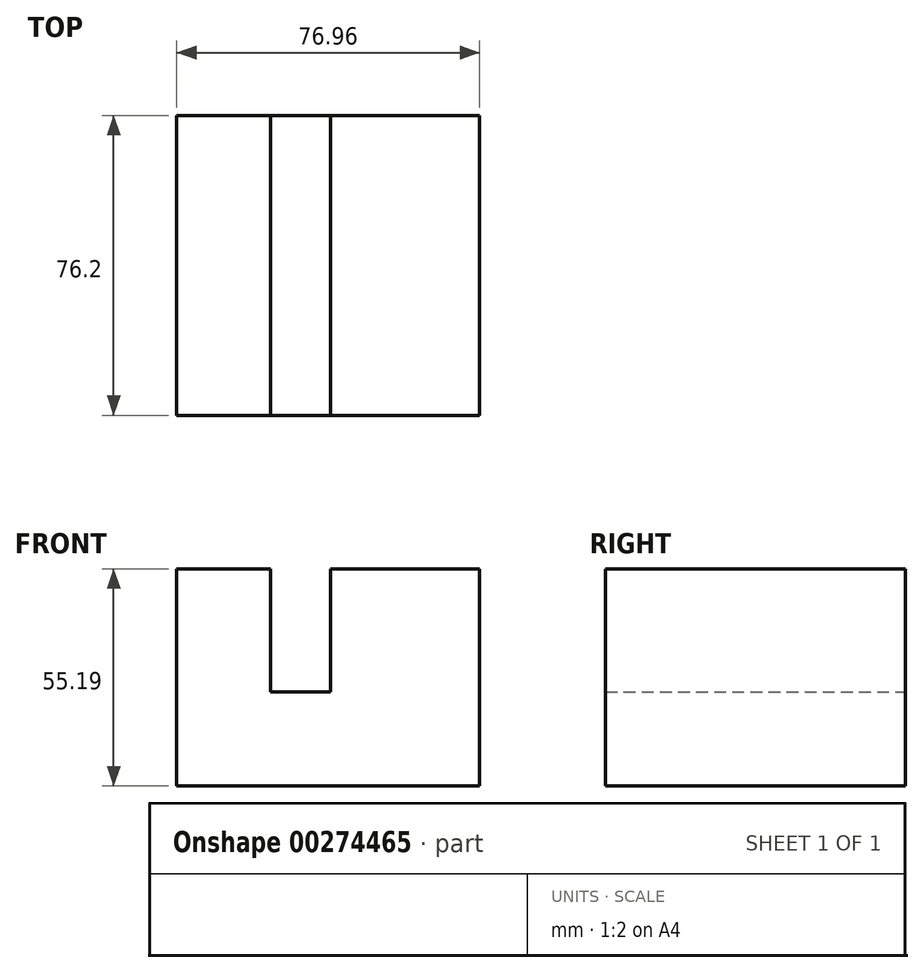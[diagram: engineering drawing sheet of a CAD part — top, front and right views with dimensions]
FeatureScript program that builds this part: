
annotation { "Feature Type Name" : "Feature", "Feature Type Description" : "" }
export const myFeature = defineFeature(function(context is Context, id is Id, definition is map)
    precondition{}
    {
        {
            var Q0;
            Q0=qCreatedBy(makeId("Front.planeOp"),FACE);
            var sketch = newSketch(context, id + "F0", { "sketchPlane" : qUnion([Q0])});
            skLineSegment(sketch, "E0", {"start": v(0, 0) * mm, "end": v(-76.96, 0) * mm});
            skLineSegment(sketch, "E1", {"start": v(-76.96, 0) * mm, "end": v(-76.96, 55.2) * mm});
            skLineSegment(sketch, "E2", {"start": v(-76.96, 55.2) * mm, "end": v(-53.09, 55.2) * mm});
            skLineSegment(sketch, "E3", {"start": v(-53.09, 55.2) * mm, "end": v(-53.09, 23.88) * mm});
            skLineSegment(sketch, "E4", {"start": v(-53.09, 23.88) * mm, "end": v(-37.82, 23.88) * mm});
            skLineSegment(sketch, "E5", {"start": v(-37.82, 23.88) * mm, "end": v(-37.82, 55.2) * mm});
            skLineSegment(sketch, "E6", {"start": v(-37.82, 55.2) * mm, "end": v(0, 55.2) * mm});
            skLineSegment(sketch, "E7", {"start": v(0, 55.2) * mm, "end": v(0, 0) * mm});
            skSolve(sketch);
        }
        {
            var Q0;
            Q0 = qSketchRegion(id + "F0", true);
            extrude(context, id + "F1", {"entities" : qUnion([Q0]), "depth" : 76.2 * mm});
        }
    });
